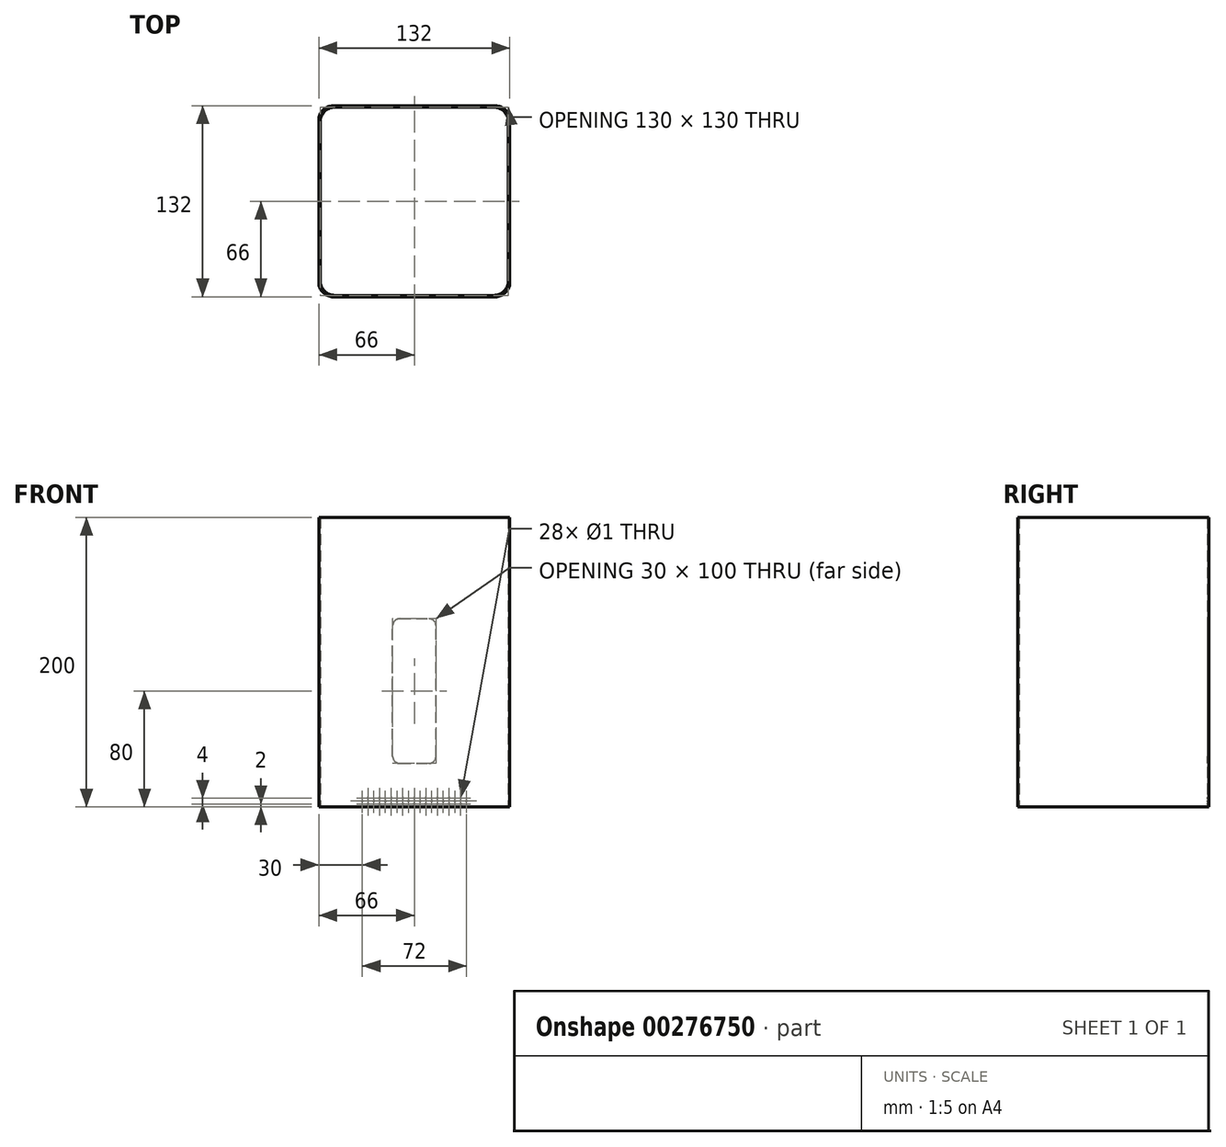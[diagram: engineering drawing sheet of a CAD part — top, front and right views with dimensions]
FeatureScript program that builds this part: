
annotation { "Feature Type Name" : "Feature", "Feature Type Description" : "" }
export const myFeature = defineFeature(function(context is Context, id is Id, definition is map)
    precondition{}
    {
        {
            var Q0;
            Q0=qCreatedBy(makeId("Top.planeOp"),FACE);
            var sketch = newSketch(context, id + "F0", { "sketchPlane" : qUnion([Q0])});
            skLineSegment(sketch, "E0.bottom", {"start": v(56, -66) * mm, "end": v(-56, -66) * mm});
            skLineSegment(sketch, "E0.top", {"start": v(56, 66) * mm, "end": v(-56, 66) * mm});
            skLineSegment(sketch, "E0.left", {"start": v(66, -56) * mm, "end": v(66, 56) * mm});
            skLineSegment(sketch, "E0.right", {"start": v(-66, -56) * mm, "end": v(-66, 56) * mm});
            skPoint(sketch, "E0.middle", {"position": v(0, 0) * mm});
            skPoint(sketch, "E1.visualSharp", {"position": v(-66, 66) * mm});
            skArc(sketch, "E1.filletArc", {"start": v(-56, 66) * mm, "mid": v(-63.07, 63.07) * mm, "end": v(-66, 56) * mm});
            skPoint(sketch, "E2.visualSharp", {"position": v(66, 66) * mm});
            skArc(sketch, "E2.filletArc", {"start": v(66, 56) * mm, "mid": v(63.07, 63.07) * mm, "end": v(56, 66) * mm});
            skPoint(sketch, "E3.visualSharp", {"position": v(66, -66) * mm});
            skArc(sketch, "E3.filletArc", {"start": v(56, -66) * mm, "mid": v(63.07, -63.07) * mm, "end": v(66, -56) * mm});
            skPoint(sketch, "E4.visualSharp", {"position": v(-66, -66) * mm});
            skArc(sketch, "E4.filletArc", {"start": v(-66, -56) * mm, "mid": v(-63.07, -63.07) * mm, "end": v(-56, -66) * mm});
            skLineSegment(sketch, "E5.0", {"start": v(55, 65) * mm, "end": v(-55, 65) * mm});
            skLineSegment(sketch, "E5.1", {"start": v(65, -55) * mm, "end": v(65, 55) * mm});
            skLineSegment(sketch, "E5.2", {"start": v(55, -65) * mm, "end": v(-55, -65) * mm});
            skLineSegment(sketch, "E5.3", {"start": v(-65, -55) * mm, "end": v(-65, 55) * mm});
            skPoint(sketch, "E6.visualSharp", {"position": v(-65, 65) * mm});
            skArc(sketch, "E6.filletArc", {"start": v(-55, 65) * mm, "mid": v(-62.07, 62.07) * mm, "end": v(-65, 55) * mm});
            skPoint(sketch, "E7.visualSharp", {"position": v(65, 65) * mm});
            skArc(sketch, "E7.filletArc", {"start": v(65, 55) * mm, "mid": v(62.07, 62.07) * mm, "end": v(55, 65) * mm});
            skPoint(sketch, "E8.visualSharp", {"position": v(65, -65) * mm});
            skArc(sketch, "E8.filletArc", {"start": v(55, -65) * mm, "mid": v(62.07, -62.07) * mm, "end": v(65, -55) * mm});
            skPoint(sketch, "E9.visualSharp", {"position": v(-65, -65) * mm});
            skArc(sketch, "E9.filletArc", {"start": v(-65, -55) * mm, "mid": v(-62.07, -62.07) * mm, "end": v(-55, -65) * mm});
            skSolve(sketch);
        }
        {
            var Q0;
            Q0=makeQuery(id+"F0.imprint","IMPRINT",FACE,{"disambiguationData":[TD([[makeQuery(id+"F0.imprint","IMPRINT",EDGE,{"derivedFrom":sQuery(id+"F0.wireOp",EDGE,"E0.bottom")}),-1.0]])]});
            extrude(context, id + "F1", {"entities" : qUnion([Q0]), "depth" : 200 * mm});
        }
        {
            var Q0;
            Q0=makeQuery(id+"F1.opExtrude","SWEPT_FACE",FACE,{"disambiguationData":[OSD([sQuery(id+"F0.wireOp",EDGE,"E0.top")])]});
            var sketch = newSketch(context, id + "F2", { "sketchPlane" : qUnion([Q0])});
            skLineSegment(sketch, "E10.bottom", {"start": v(10, 30) * mm, "end": v(-10, 30) * mm});
            skLineSegment(sketch, "E10.top", {"start": v(10, 130) * mm, "end": v(-10, 130) * mm});
            skLineSegment(sketch, "E10.left", {"start": v(15, 35) * mm, "end": v(15, 125) * mm});
            skLineSegment(sketch, "E10.right", {"start": v(-15, 35) * mm, "end": v(-15, 125) * mm});
            skPoint(sketch, "E10.middle", {"position": v(0, 80) * mm});
            skPoint(sketch, "E11.visualSharp", {"position": v(-15, 130) * mm});
            skArc(sketch, "E11.filletArc", {"start": v(-10, 130) * mm, "mid": v(-13.54, 128.54) * mm, "end": v(-15, 125) * mm});
            skPoint(sketch, "E12.visualSharp", {"position": v(15, 130) * mm});
            skArc(sketch, "E12.filletArc", {"start": v(15, 125) * mm, "mid": v(13.54, 128.54) * mm, "end": v(10, 130) * mm});
            skPoint(sketch, "E13.visualSharp", {"position": v(15, 30) * mm});
            skArc(sketch, "E13.filletArc", {"start": v(10, 30) * mm, "mid": v(13.54, 31.46) * mm, "end": v(15, 35) * mm});
            skPoint(sketch, "E14.visualSharp", {"position": v(-15, 30) * mm});
            skArc(sketch, "E14.filletArc", {"start": v(-15, 35) * mm, "mid": v(-13.54, 31.46) * mm, "end": v(-10, 30) * mm});
            skSolve(sketch);
        }
        {
            var Q0;
            Q0=makeQuery(id+"F2.imprint","IMPRINT",FACE,{"disambiguationData":[TD([[makeQuery(id+"F2.imprint","IMPRINT",EDGE,{"derivedFrom":sQuery(id+"F2.wireOp",EDGE,"E10.bottom")}),-1.0]])]});
            extrude(context, id + "F3", {"entities" : qUnion([Q0]), "operationType" : NewBodyOperationType.REMOVE, "oppositeDirection" : true, "depth" : 25 * mm});
        }
        {
            var Q0;
            Q0=makeQuery(id+"F1.opExtrude","SWEPT_FACE",FACE,{"disambiguationData":[OSD([sQuery(id+"F0.wireOp",EDGE,"E0.top")])]});
            var sketch = newSketch(context, id + "F4", { "sketchPlane" : qUnion([Q0])});
            skCircle(sketch, "E15", {"center": v(0, 6) * mm, "radius": 0.5 * mm});
            skCircle(sketch, "E16", {"center": v(4, 4) * mm, "radius": 0.5 * mm});
            skCircle(sketch, "E17", {"center": v(8, 2) * mm, "radius": 0.5 * mm});
            skCircle(sketch, "E18.1.0.0", {"center": v(16, 2) * mm, "radius": 0.5 * mm});
            skCircle(sketch, "E18.1.0.1", {"center": v(12, 4) * mm, "radius": 0.5 * mm});
            skCircle(sketch, "E18.1.0.2", {"center": v(8, 6) * mm, "radius": 0.5 * mm});
            skCircle(sketch, "E18.2.0.0", {"center": v(24, 2) * mm, "radius": 0.5 * mm});
            skCircle(sketch, "E18.2.0.1", {"center": v(20, 4) * mm, "radius": 0.5 * mm});
            skCircle(sketch, "E18.2.0.2", {"center": v(16, 6) * mm, "radius": 0.5 * mm});
            skCircle(sketch, "E18.3.0.0", {"center": v(32, 2) * mm, "radius": 0.5 * mm});
            skCircle(sketch, "E18.3.0.1", {"center": v(28, 4) * mm, "radius": 0.5 * mm});
            skCircle(sketch, "E18.3.0.2", {"center": v(24, 6) * mm, "radius": 0.5 * mm});
            skLineSegment(sketch, "E18.direction1", {"start": v(8, 2) * mm, "end": v(16, 2) * mm, "construction": true});
            skCircle(sketch, "E19.1.0.0", {"center": v(-8, 6) * mm, "radius": 0.5 * mm});
            skCircle(sketch, "E19.1.0.1", {"center": v(-4, 4) * mm, "radius": 0.5 * mm});
            skCircle(sketch, "E19.1.0.2", {"center": v(0, 2) * mm, "radius": 0.5 * mm});
            skCircle(sketch, "E19.2.0.0", {"center": v(-16, 6) * mm, "radius": 0.5 * mm});
            skCircle(sketch, "E19.2.0.1", {"center": v(-12, 4) * mm, "radius": 0.5 * mm});
            skCircle(sketch, "E19.2.0.2", {"center": v(-8, 2) * mm, "radius": 0.5 * mm});
            skCircle(sketch, "E19.3.0.0", {"center": v(-24, 6) * mm, "radius": 0.5 * mm});
            skCircle(sketch, "E19.3.0.1", {"center": v(-20, 4) * mm, "radius": 0.5 * mm});
            skCircle(sketch, "E19.3.0.2", {"center": v(-16, 2) * mm, "radius": 0.5 * mm});
            skCircle(sketch, "E19.4.0.0", {"center": v(-32, 6) * mm, "radius": 0.5 * mm});
            skCircle(sketch, "E19.4.0.1", {"center": v(-28, 4) * mm, "radius": 0.5 * mm});
            skCircle(sketch, "E19.4.0.2", {"center": v(-24, 2) * mm, "radius": 0.5 * mm});
            skLineSegment(sketch, "E19.direction1", {"start": v(0, 6) * mm, "end": v(-8, 6) * mm, "construction": true});
            skCircle(sketch, "E20", {"center": v(-32, 2) * mm, "radius": 0.5 * mm});
            skCircle(sketch, "E21", {"center": v(32, 6) * mm, "radius": 0.5 * mm});
            skCircle(sketch, "E22.1.0.0", {"center": v(-36, 4) * mm, "radius": 0.5 * mm});
            skLineSegment(sketch, "E22.direction1", {"start": v(-28, 4) * mm, "end": v(-36, 4) * mm, "construction": true});
            skCircle(sketch, "E23.1.0.0", {"center": v(36, 4) * mm, "radius": 0.5 * mm});
            skLineSegment(sketch, "E23.direction1", {"start": v(28, 4) * mm, "end": v(36, 4) * mm, "construction": true});
            skSolve(sketch);
        }
        {
            var Q0;
            Q0=makeQuery(id+"F4.imprint","IMPRINT",FACE,{"disambiguationData":[TD([[makeQuery(id+"F4.imprint","IMPRINT",EDGE,{"derivedFrom":sQuery(id+"F4.wireOp",EDGE,"E19.1.0.2")}),1.0]])]});
            var Q1;
            Q1=makeQuery(id+"F4.imprint","IMPRINT",FACE,{"disambiguationData":[TD([[makeQuery(id+"F4.imprint","IMPRINT",EDGE,{"derivedFrom":sQuery(id+"F4.wireOp",EDGE,"E19.1.0.1")}),1.0]])]});
            var Q2;
            Q2=makeQuery(id+"F4.imprint","IMPRINT",FACE,{"disambiguationData":[TD([[makeQuery(id+"F4.imprint","IMPRINT",EDGE,{"derivedFrom":sQuery(id+"F4.wireOp",EDGE,"E19.2.0.0")}),1.0]])]});
            var Q3;
            Q3=makeQuery(id+"F4.imprint","IMPRINT",FACE,{"disambiguationData":[TD([[makeQuery(id+"F4.imprint","IMPRINT",EDGE,{"derivedFrom":sQuery(id+"F4.wireOp",EDGE,"E19.2.0.2")}),1.0]])]});
            var Q4;
            Q4=makeQuery(id+"F4.imprint","IMPRINT",FACE,{"disambiguationData":[TD([[makeQuery(id+"F4.imprint","IMPRINT",EDGE,{"derivedFrom":sQuery(id+"F4.wireOp",EDGE,"E19.4.0.0")}),1.0]])]});
            var Q5;
            Q5=makeQuery(id+"F4.imprint","IMPRINT",FACE,{"disambiguationData":[TD([[makeQuery(id+"F4.imprint","IMPRINT",EDGE,{"derivedFrom":sQuery(id+"F4.wireOp",EDGE,"E19.2.0.1")}),1.0]])]});
            var Q6;
            Q6=makeQuery(id+"F4.imprint","IMPRINT",FACE,{"disambiguationData":[TD([[makeQuery(id+"F4.imprint","IMPRINT",EDGE,{"derivedFrom":sQuery(id+"F4.wireOp",EDGE,"E19.4.0.2")}),1.0]])]});
            var Q7;
            Q7=makeQuery(id+"F4.imprint","IMPRINT",FACE,{"disambiguationData":[TD([[makeQuery(id+"F4.imprint","IMPRINT",EDGE,{"derivedFrom":sQuery(id+"F4.wireOp",EDGE,"E16")}),1.0]])]});
            var Q8;
            Q8=makeQuery(id+"F4.imprint","IMPRINT",FACE,{"disambiguationData":[TD([[makeQuery(id+"F4.imprint","IMPRINT",EDGE,{"derivedFrom":sQuery(id+"F4.wireOp",EDGE,"E18.1.0.1")}),1.0]])]});
            var Q9;
            Q9=makeQuery(id+"F4.imprint","IMPRINT",FACE,{"disambiguationData":[TD([[makeQuery(id+"F4.imprint","IMPRINT",EDGE,{"derivedFrom":sQuery(id+"F4.wireOp",EDGE,"E18.2.0.0")}),1.0]])]});
            var Q10;
            Q10=makeQuery(id+"F4.imprint","IMPRINT",FACE,{"disambiguationData":[TD([[makeQuery(id+"F4.imprint","IMPRINT",EDGE,{"derivedFrom":sQuery(id+"F4.wireOp",EDGE,"E18.2.0.1")}),1.0]])]});
            var Q11;
            Q11=makeQuery(id+"F4.imprint","IMPRINT",FACE,{"disambiguationData":[TD([[makeQuery(id+"F4.imprint","IMPRINT",EDGE,{"derivedFrom":sQuery(id+"F4.wireOp",EDGE,"E18.2.0.2")}),1.0]])]});
            var Q12;
            Q12=makeQuery(id+"F4.imprint","IMPRINT",FACE,{"disambiguationData":[TD([[makeQuery(id+"F4.imprint","IMPRINT",EDGE,{"derivedFrom":sQuery(id+"F4.wireOp",EDGE,"E18.3.0.0")}),1.0]])]});
            var Q13;
            Q13=makeQuery(id+"F4.imprint","IMPRINT",FACE,{"disambiguationData":[TD([[makeQuery(id+"F4.imprint","IMPRINT",EDGE,{"derivedFrom":sQuery(id+"F4.wireOp",EDGE,"E18.3.0.2")}),1.0]])]});
            var Q14;
            Q14=makeQuery(id+"F4.imprint","IMPRINT",FACE,{"disambiguationData":[TD([[makeQuery(id+"F4.imprint","IMPRINT",EDGE,{"derivedFrom":sQuery(id+"F4.wireOp",EDGE,"E19.3.0.2")}),1.0]])]});
            var Q15;
            Q15=makeQuery(id+"F4.imprint","IMPRINT",FACE,{"disambiguationData":[TD([[makeQuery(id+"F4.imprint","IMPRINT",EDGE,{"derivedFrom":sQuery(id+"F4.wireOp",EDGE,"E19.3.0.0")}),1.0]])]});
            var Q16;
            Q16=makeQuery(id+"F4.imprint","IMPRINT",FACE,{"disambiguationData":[TD([[makeQuery(id+"F4.imprint","IMPRINT",EDGE,{"derivedFrom":sQuery(id+"F4.wireOp",EDGE,"E19.3.0.1")}),1.0]])]});
            var Q17;
            Q17=makeQuery(id+"F4.imprint","IMPRINT",FACE,{"disambiguationData":[TD([[makeQuery(id+"F4.imprint","IMPRINT",EDGE,{"derivedFrom":sQuery(id+"F4.wireOp",EDGE,"E17")}),1.0]])]});
            var Q18;
            Q18=makeQuery(id+"F4.imprint","IMPRINT",FACE,{"disambiguationData":[TD([[makeQuery(id+"F4.imprint","IMPRINT",EDGE,{"derivedFrom":sQuery(id+"F4.wireOp",EDGE,"E19.4.0.1")}),1.0]])]});
            var Q19;
            Q19=makeQuery(id+"F4.imprint","IMPRINT",FACE,{"disambiguationData":[TD([[makeQuery(id+"F4.imprint","IMPRINT",EDGE,{"derivedFrom":sQuery(id+"F4.wireOp",EDGE,"E18.1.0.0")}),1.0]])]});
            var Q20;
            Q20=makeQuery(id+"F4.imprint","IMPRINT",FACE,{"disambiguationData":[TD([[makeQuery(id+"F4.imprint","IMPRINT",EDGE,{"derivedFrom":sQuery(id+"F4.wireOp",EDGE,"E18.1.0.2")}),1.0]])]});
            var Q21;
            Q21=makeQuery(id+"F4.imprint","IMPRINT",FACE,{"disambiguationData":[TD([[makeQuery(id+"F4.imprint","IMPRINT",EDGE,{"derivedFrom":sQuery(id+"F4.wireOp",EDGE,"E18.3.0.1")}),1.0]])]});
            var Q22;
            Q22=makeQuery(id+"F4.imprint","IMPRINT",FACE,{"disambiguationData":[TD([[makeQuery(id+"F4.imprint","IMPRINT",EDGE,{"derivedFrom":sQuery(id+"F4.wireOp",EDGE,"E19.1.0.0")}),1.0]])]});
            var Q23;
            Q23=makeQuery(id+"F4.imprint","IMPRINT",FACE,{"disambiguationData":[TD([[makeQuery(id+"F4.imprint","IMPRINT",EDGE,{"derivedFrom":sQuery(id+"F4.wireOp",EDGE,"E15")}),1.0]])]});
            var Q24;
            Q24=makeQuery(id+"F4.imprint","IMPRINT",FACE,{"disambiguationData":[TD([[makeQuery(id+"F4.imprint","IMPRINT",EDGE,{"derivedFrom":sQuery(id+"F4.wireOp",EDGE,"E21")}),1.0]])]});
            var Q25;
            Q25=makeQuery(id+"F4.imprint","IMPRINT",FACE,{"disambiguationData":[TD([[makeQuery(id+"F4.imprint","IMPRINT",EDGE,{"derivedFrom":sQuery(id+"F4.wireOp",EDGE,"E20")}),1.0]])]});
            var Q26;
            Q26=makeQuery(id+"F4.imprint","IMPRINT",FACE,{"disambiguationData":[TD([[makeQuery(id+"F4.imprint","IMPRINT",EDGE,{"derivedFrom":sQuery(id+"F4.wireOp",EDGE,"E23.1.0.0")}),1.0]])]});
            var Q27;
            Q27=makeQuery(id+"F4.imprint","IMPRINT",FACE,{"disambiguationData":[TD([[makeQuery(id+"F4.imprint","IMPRINT",EDGE,{"derivedFrom":sQuery(id+"F4.wireOp",EDGE,"E22.1.0.0")}),1.0]])]});
            extrude(context, id + "F5", {"entities" : qUnion([Q0, Q1, Q2, Q3, Q4, Q5, Q6, Q7, Q8, Q9, Q10, Q11, Q12, Q13, Q14, Q15, Q16, Q17, Q18, Q19, Q20, Q21, Q22, Q23, Q24, Q25, Q26, Q27]), "operationType" : NewBodyOperationType.REMOVE, "oppositeDirection" : true, "depth" : 2 * mm});
        }
    });
